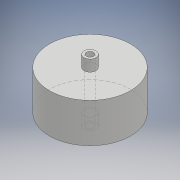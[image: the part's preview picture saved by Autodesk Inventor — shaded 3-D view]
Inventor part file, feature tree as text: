
AUTODESK INVENTOR PART (.ipt)
format: ipt  version: 2018 (Build 220112000, 112)  size: 103,936 bytes
history: native  units: mm
features: sketch x3, extrude x2, other x1, hole x1
ambient origin geometry x8: Origin, YZ Plane, XZ Plane, XY Plane, X Axis, Y Axis, Z Axis, Center Point
bodies: Body1 (feature_tree)
feature tree (7):
  other  "ソリッド1"
  extrude  "押し出し1"  Depth=136.0mm
  extrude  "押し出し2"  Depth=66.0mm TaperAngle=0.0deg
  hole  "穴1"  [1 undecoded]
  sketch  "スケッチ1"
  sketch  "スケッチ2"
  sketch  "スケッチ3"
note: 1 required parameter value undecoded (feature->parameter linkage not recoverable at this tier; creation-order binding heuristic only, values carry confidence <= 0.55)
